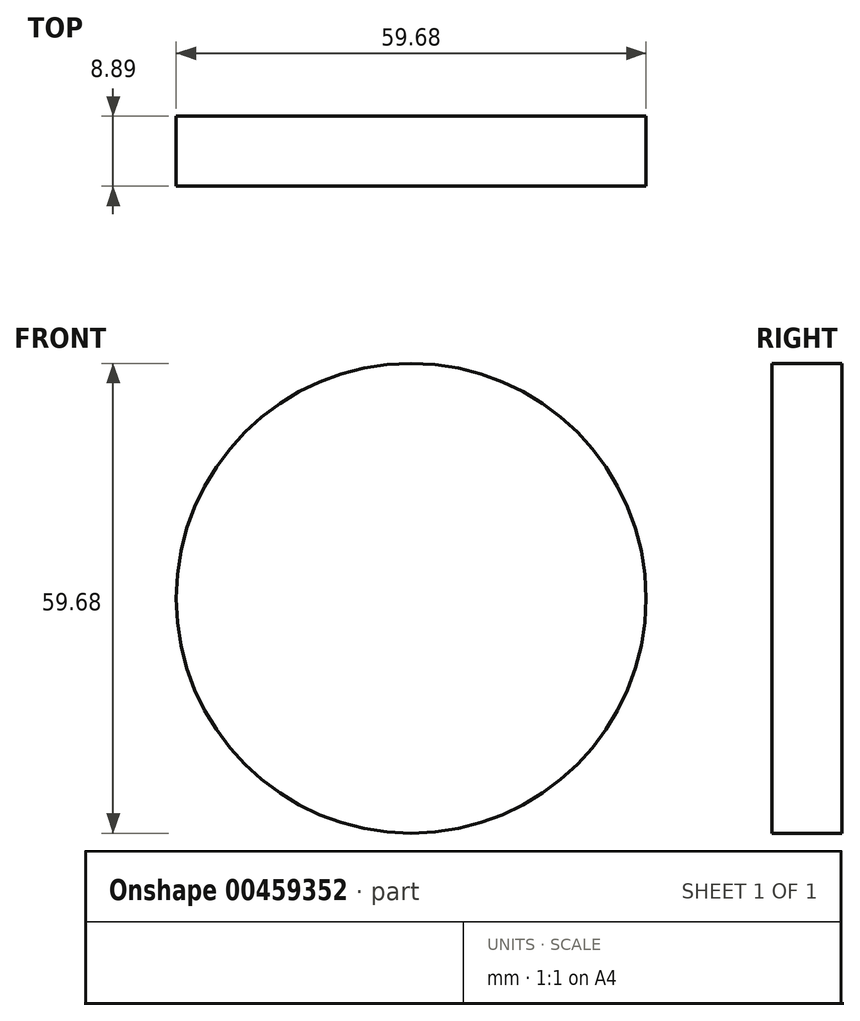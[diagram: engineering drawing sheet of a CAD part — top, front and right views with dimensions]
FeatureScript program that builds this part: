
annotation { "Feature Type Name" : "Feature", "Feature Type Description" : "" }
export const myFeature = defineFeature(function(context is Context, id is Id, definition is map)
    precondition{}
    {
        {
            var Q0;
            Q0=qCreatedBy(makeId("Front.planeOp"),FACE);
            var sketch = newSketch(context, id + "F0", { "sketchPlane" : qUnion([Q0])});
            skCircle(sketch, "E0", {"center": v(0, 0) * mm, "radius": 29.84 * mm});
            skSolve(sketch);
        }
        {
            var Q0;
            Q0 = qSketchRegion(id + "F0", true);
            extrude(context, id + "F1", {"entities" : qUnion([Q0]), "depth" : 8.9 * mm});
        }
    });
